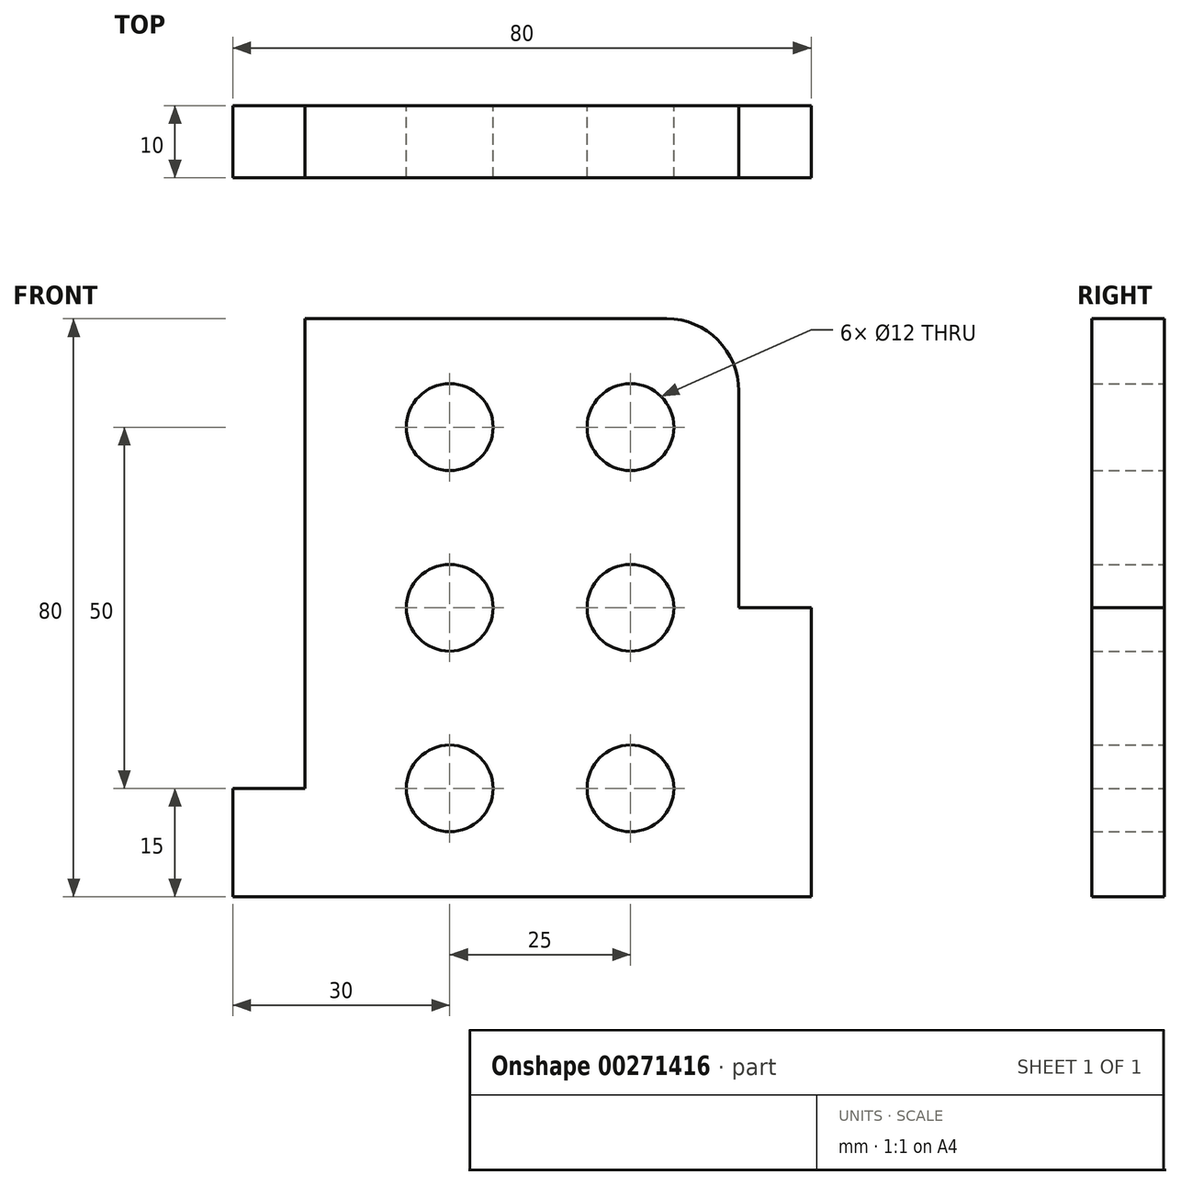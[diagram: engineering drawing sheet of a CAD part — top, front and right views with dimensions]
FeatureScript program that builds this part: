
annotation { "Feature Type Name" : "Feature", "Feature Type Description" : "" }
export const myFeature = defineFeature(function(context is Context, id is Id, definition is map)
    precondition{}
    {
        {
            var Q0;
            Q0=qCreatedBy(makeId("Front.planeOp"),FACE);
            var sketch = newSketch(context, id + "F0", { "sketchPlane" : qUnion([Q0])});
            skLineSegment(sketch, "E0", {"start": v(0, 0) * mm, "end": v(80, 0) * mm});
            skLineSegment(sketch, "E1", {"start": v(80, 0) * mm, "end": v(80, 40) * mm});
            skLineSegment(sketch, "E2", {"start": v(80, 40) * mm, "end": v(70, 40) * mm});
            skLineSegment(sketch, "E3", {"start": v(70, 40) * mm, "end": v(70, 70) * mm});
            skLineSegment(sketch, "E4", {"start": v(0, 0) * mm, "end": v(0, 15) * mm});
            skLineSegment(sketch, "E5", {"start": v(0, 15) * mm, "end": v(10, 15) * mm});
            skLineSegment(sketch, "E6", {"start": v(10, 15) * mm, "end": v(10, 80) * mm});
            skLineSegment(sketch, "E7", {"start": v(10, 80) * mm, "end": v(60, 80) * mm});
            skPoint(sketch, "E8.visualSharp", {"position": v(70, 80) * mm});
            skArc(sketch, "E8.filletArc", {"start": v(70, 70) * mm, "mid": v(67.07, 77.07) * mm, "end": v(60, 80) * mm});
            skCircle(sketch, "E9", {"center": v(55, 15) * mm, "radius": 6 * mm});
            skCircle(sketch, "E10", {"center": v(30, 15) * mm, "radius": 6 * mm});
            skCircle(sketch, "E11", {"center": v(55, 40) * mm, "radius": 6 * mm});
            skCircle(sketch, "E12", {"center": v(30, 40) * mm, "radius": 6 * mm});
            skCircle(sketch, "E13", {"center": v(55, 65) * mm, "radius": 6 * mm});
            skCircle(sketch, "E14", {"center": v(30, 65) * mm, "radius": 6 * mm});
            skSolve(sketch);
        }
        {
            var Q0;
            Q0 = qSketchRegion(id + "F0", true);
            extrude(context, id + "F1", {"entities" : qUnion([Q0]), "depth" : 10 * mm});
        }
    });
